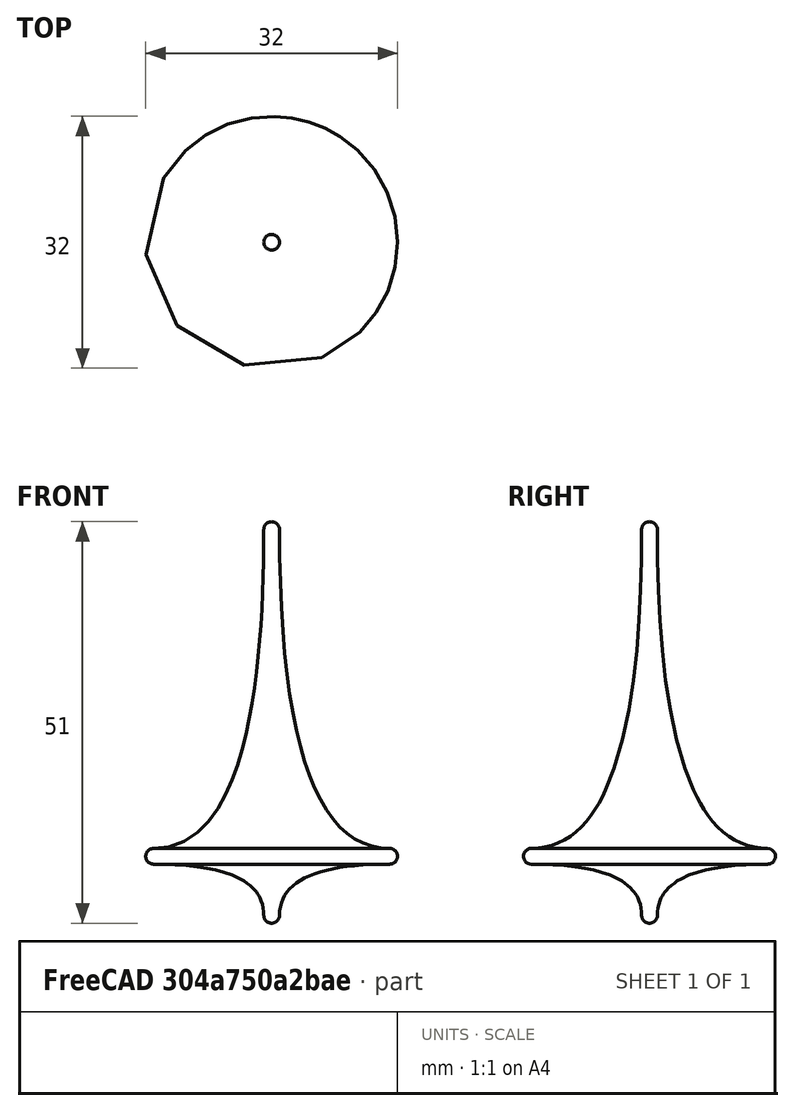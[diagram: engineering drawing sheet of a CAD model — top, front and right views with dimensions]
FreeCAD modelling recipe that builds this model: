
FCSTD DOCUMENT  (FreeCAD 0.21R33694 (Git))
Label: top
License: All rights reserved
LicenseURL: https://en.wikipedia.org/wiki/All_rights_reserved
objects: Sketcher::SketchObject×1, PartDesign::Revolution×1, PartDesign::Body×1
note: 4 computed .brp shape members not serialized (recipe doc carries the construction recipe); baked Part::Feature solids carry a one-line shape summary decoded from their .brp

FEATURE [Sketcher::SketchObject] Sketch
  FullyConstrained = true
  MapMode = 5
  Placement = pos=(0,0,0) rot=(1,0,0;1.5708rad)
  Support = -> [XZ_Plane]
  sketch-geometry (18):
    g0: ArcOfCircle CenterX=0 CenterY=0 CenterZ=0 NormalX=0 NormalY=0 NormalZ=1 AngleXU=0 Radius=1 StartAngle=4.71239 EndAngle=6.28319
    g1: GeomPoint X=15 Y=7.5 Z=0
    g2: ArcOfCircle CenterX=15 CenterY=7.5 CenterZ=0 NormalX=0 NormalY=0 NormalZ=1 AngleXU=0 Radius=1 StartAngle=4.71239 EndAngle=7.85398
    g3: Circle CenterX=1 CenterY=6e-16 CenterZ=0 NormalX=0 NormalY=0 NormalZ=1 AngleXU=0 Radius=1
    g4: Circle CenterX=1 CenterY=6.5 CenterZ=0 NormalX=0 NormalY=0 NormalZ=1 AngleXU=0 Radius=1
    g5: Circle CenterX=15 CenterY=6.5 CenterZ=0 NormalX=0 NormalY=0 NormalZ=1 AngleXU=0 Radius=1
    g6: BSplineCurve PolesCount=3 KnotsCount=2 Degree=2 IsPeriodic=0
    g7: GeomPoint X=1 Y=0 Z=0
    g8: GeomPoint X=15 Y=6.5 Z=0
    g9: GeomPoint X=0 Y=49 Z=0
    g10: ArcOfCircle CenterX=0 CenterY=49 CenterZ=0 NormalX=0 NormalY=0 NormalZ=1 AngleXU=0 Radius=1 StartAngle=0 EndAngle=1.5708
    g11: Circle CenterX=15 CenterY=8.5 CenterZ=0 NormalX=0 NormalY=0 NormalZ=1 AngleXU=0 Radius=1
    g12: Circle CenterX=1 CenterY=8.5 CenterZ=0 NormalX=0 NormalY=0 NormalZ=1 AngleXU=0 Radius=1
    g13: Circle CenterX=1 CenterY=49 CenterZ=0 NormalX=0 NormalY=0 NormalZ=1 AngleXU=0 Radius=1
    g14: BSplineCurve PolesCount=3 KnotsCount=2 Degree=2 IsPeriodic=0
    g15: GeomPoint X=15 Y=8.5 Z=0
    g16: GeomPoint X=1 Y=49 Z=0
    g17: LineSegment StartX=0 StartY=-1 StartZ=0 EndX=0 EndY=50 EndZ=0
  constraints (42):
    c: Coincident(g0,g-1)
    c: PointOnObject(g0,g-1)
    c: PointOnObject(g0,g-2)
    c: DistanceY(g0,g0) = 1
    c: DistanceY(g0,g1) = 7.5
    c: DistanceX(g0,g1) = 15
    c: Coincident(g2,g1)
    c: Vertical(g2,g2)
    c: Vertical(g2,g2)
    c: DistanceY(g2,g2) = 1
    c: Weight(g3) = 1
    c: Coincident(g6,g0)
    c: Equal(g3,g4)
    c: Equal(g3,g5)
    c: Coincident(g6,g2)
    c: InternalAlignment(g3,g6)
    c: InternalAlignment(g4,g6)
    c: InternalAlignment(g5,g6)
    c: InternalAlignment(g7,g6)
    c: InternalAlignment(g8,g6)
    c: Vertical(g9,g0)
    c: Coincident(g10,g9)
    c: Horizontal(g10,g10)
    c: Vertical(g10,g10)
    c: Equal(g10,g0)
    c: Weight(g11) = 1
    c: Coincident(g14,g2)
    c: Equal(g11,g12)
    c: Equal(g11,g13)
    c: Coincident(g14,g10)
    c: InternalAlignment(g11,g14)
    c: InternalAlignment(g12,g14)
    c: InternalAlignment(g13,g14)
    c: InternalAlignment(g15,g14)
    c: InternalAlignment(g16,g14)
    c: DistanceY(g0,g10) = 50
    c: Coincident(g17,g0)
    c: Coincident(g17,g10)
    c: Vertical(g4,g12)
    c: Horizontal(g2,g12)
    c: Horizontal(g4,g2)
    c: Vertical(g12,g10)
FEATURE [PartDesign::Revolution] Revolution
  Angle = 360
  Axis = (0,2e-16,1)
  Base = (0,0,0)
  Placement = pos=(0,0,0) rot=(1,0,0;1.5708rad)
  Profile = -> Sketch
  ReferenceAxis = -> Sketch [V_Axis]
  Reversed = true
FEATURE [PartDesign::Body] Body
  Group = -> [Sketch,Revolution]
  Origin = -> Origin
  Tip = -> Revolution
